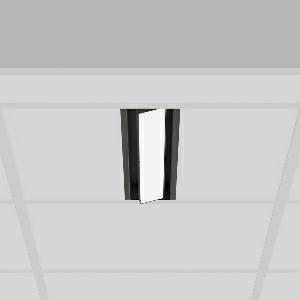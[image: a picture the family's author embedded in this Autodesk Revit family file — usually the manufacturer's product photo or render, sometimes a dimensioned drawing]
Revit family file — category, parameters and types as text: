
# Revit family: tx-move_901727_003_1_45c0
name_source: partatom
category: Lighting Fixtures
units: mm (PartAtom-declared; Revit-internal decimal feet)

## family parameters
Cut with Voids When Loaded = No
Host = Face
Light Source = No
Part Type = Normal
Room Calculation Point = No
Round Connector Dimension = Use Diameter
Shared = No

## types (1)
- MultiLumen 1 (1 x LED Modul 840, 2550 lm, 4000)
    Apparent Load = 18 VA
    Approval mark = CE
    CIE Flux Codes = 47 79 96 100 100
    Color Rendering = 80
    Color Temperature = 4000
    Default Elevation = 1800 mm
    Description = Series: TX-MOVE
Einlege/Einbau-Flächenstrahler. Housing: sheet steel, powder-coated. Swivel range: 90°. High-efficiency LED units with flush-mounted opal diffuser made of non-yellowing PMMA. Symmetrical wide beam light emission. Suitable for laying in grid ceiling module 600. Connected converter included in separate gearbox.Suitable for through-wiring.MultiLumen: Luminous flux adjustable in 3 steps. Accessories: Mounting frame for installation in suspended ceilings. Environmentally friendly and resource-saving due to replaceable and recyclable components. 
Colour: deep black, matt (RAL 9005)
Length: 597 mm
Width: 116 mm
Height: 39 mm
Cut-out length: 577 mm
Cut-out width: 98 mm
Recess height: 100 mm
Lamp: LED
Socket: without socket
Colour temperature: 4000K
Colour rendering index (CRI): 80
System power: 18 W
Rated luminous flux: 2550 lm
Luminous efficiency: 142 lm/W
System power 2: 26 W
Rated luminous flux 2: 3500 lm
Luminous efficiency 2: 135 lm/W
System power 3: 39 W
Rated luminous flux 3: 4900 lm
Luminous efficiency 3: 126 lm/W
Control gear: Regulated power supply
Protection class: I
Type of protection: IP 20
    Height = 0 mm  [stored 0 ft]
    Lamp = 1 x LED Modul 840
    Lamp Light Flux = 2550 lm
    Lamp count = 1
    Length = 597 mm
    Lifetime = 50000 h
    Luminous efficacy = 142 lm/W
    Manufacturer = RZB
    ModVariant = No
    Model = 901727.003.1
    Mounting Place = Ceiling, Wall
    Mounting Type = Recessed
    Number of Poles = 1
    OnlyDefault = Yes
    Power Factor = 1
    Product Name = TX-MOVE
    Product group = Recessed projectors
    ProductGroupID = 401
    Protection Class = Protection class I
    Protection Degree = IP 20
    RLX_Detail_Level = 1
    RLX_Emergency_Light_Flux = 0 lm
    RLX_Emergency_Type = 0
    RLX_Emergency_Type_DB = No
    RlxData = <blob elided: 27265 chars, md5=643c94b9>
    Socket = socket
    Standby Power = 0 W
    System Light Flux = 2550 lm
    System Power = 18 W
    Type Comments = MultiLumen 1
    Type Image = 901727.003.jpg
    URL = http://relux.com
    VarID = multilumen_1
    Voltage = 230 V
    Voltage Range = 220-240 V
    Weight = 0.00 kg
    Width = 116 mm

note: [stored X ft] marks values corroborated as IEEE doubles in the binary element streams (Revit-internal decimal feet)

## geometry (parser evidence)
native form markers: Blend x4, Sweep x13
no freeform markers — native parametric forms only
